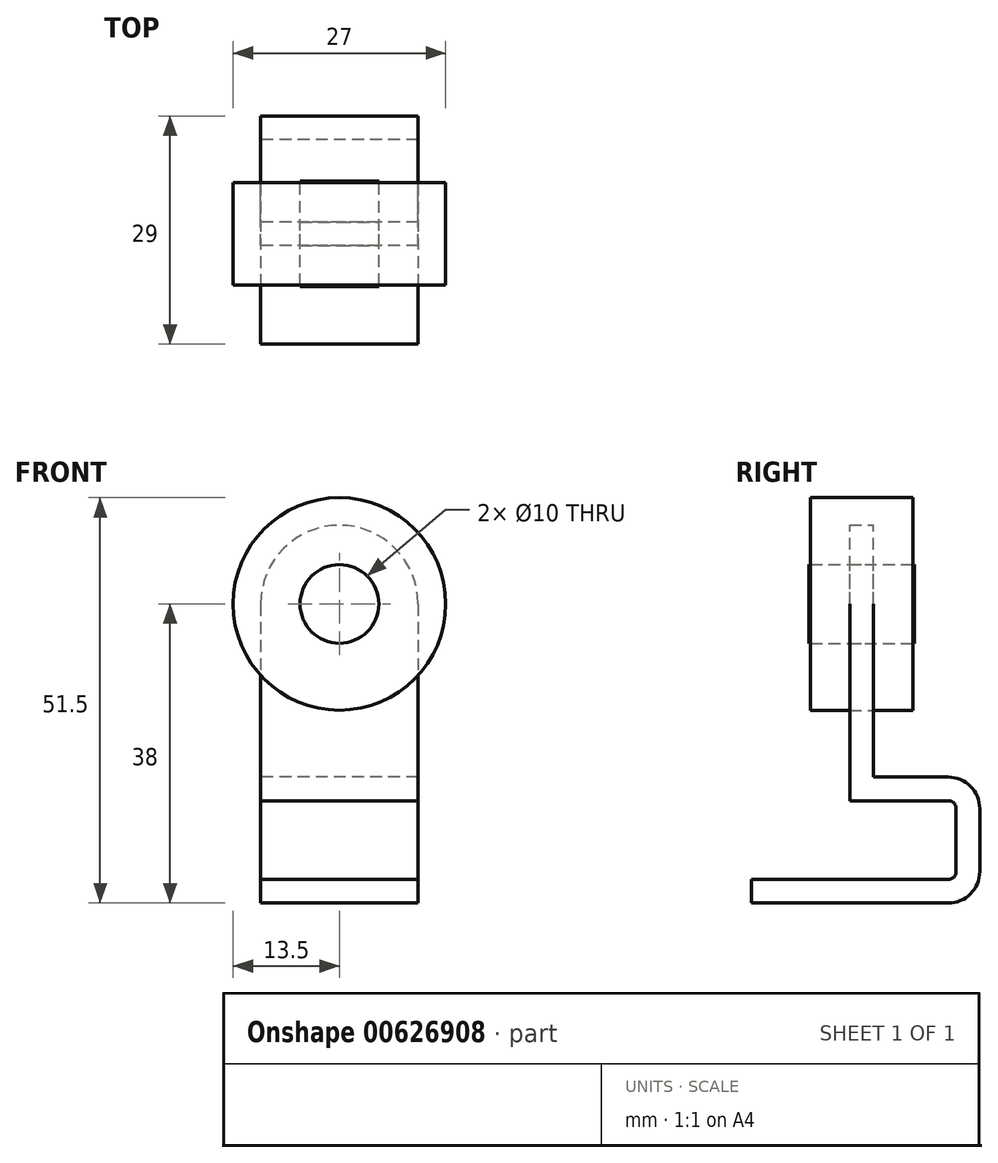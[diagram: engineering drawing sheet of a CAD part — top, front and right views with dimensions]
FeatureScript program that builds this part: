
annotation { "Feature Type Name" : "Feature", "Feature Type Description" : "" }
export const myFeature = defineFeature(function(context is Context, id is Id, definition is map)
    precondition{}
    {
        {
            var Q0;
            Q0=qCreatedBy(makeId("Front.planeOp"),FACE);
            var sketch = newSketch(context, id + "F0", { "sketchPlane" : qUnion([Q0])});
            skCircle(sketch, "E0", {"center": v(0, 0) * mm, "radius": 13.5 * mm});
            skCircle(sketch, "E1", {"center": v(0, 0) * mm, "radius": 5 * mm});
            skSolve(sketch);
        }
        {
            var Q0;
            Q0 = qSketchRegion(id + "F0", true);
            extrude(context, id + "F1", {"entities" : qUnion([Q0]), "depth" : 13 * mm, "offsetDistance" : 25 * mm, "symmetric" : true});
        }
        {
            var Q0;
            Q0=makeQuery(id+"F0.imprint","IMPRINT",FACE,{"disambiguationData":[TD([[makeQuery(id+"F0.imprint","IMPRINT",EDGE,{"derivedFrom":sQuery(id+"F0.wireOp",EDGE,"E1")}),1.0]])]});
            extrude(context, id + "F2", {"entities" : qUnion([Q0]), "depth" : 13.4 * mm, "offsetDistance" : 25 * mm, "symmetric" : true});
        }
        {
            var Q0;
            Q0=qCreatedBy(makeId("Front.planeOp"),FACE);
            var sketch = newSketch(context, id + "F3", { "sketchPlane" : qUnion([Q0])});
            skCircle(sketch, "E2.0", {"center": v(0, 0) * mm, "radius": 5 * mm});
            skArc(sketch, "E3.0", {"start": v(10, 0) * mm, "mid": v(0, 10) * mm, "end": v(-10, 0) * mm});
            skLineSegment(sketch, "E4.top", {"start": v(10, -25) * mm, "end": v(-10, -25) * mm});
            skLineSegment(sketch, "E4.left", {"start": v(10, 0) * mm, "end": v(10, -25) * mm});
            skLineSegment(sketch, "E4.right", {"start": v(-10, 0) * mm, "end": v(-10, -25) * mm});
            skLineSegment(sketch, "E5.bottom", {"start": v(-10, 0) * mm, "end": v(-10, 0) * mm});
            skLineSegment(sketch, "E5.top", {"start": v(-10, 0) * mm, "end": v(-10, 0) * mm});
            skLineSegment(sketch, "E5.left", {"start": v(-10, 0) * mm, "end": v(-10, 0) * mm});
            skLineSegment(sketch, "E5.right", {"start": v(-10, 0) * mm, "end": v(-10, 0) * mm});
            skSolve(sketch);
        }
        {
            var Q0;
            Q0 = qSketchRegion(id + "F3", true);
            extrude(context, id + "F4", {"entities" : qUnion([Q0]), "depth" : 3 * mm, "offsetDistance" : 25 * mm, "symmetric" : true});
        }
        {
            var Q0;
            Q0=qCreatedBy(makeId("Right.planeOp"),FACE);
            var sketch = newSketch(context, id + "F5", { "sketchPlane" : qUnion([Q0])});
            skLineSegment(sketch, "E6", {"start": v(0, -25) * mm, "end": v(11, -25) * mm});
            skLineSegment(sketch, "E7", {"start": v(12, -26) * mm, "end": v(12, -34) * mm});
            skLineSegment(sketch, "E8", {"start": v(11, -35) * mm, "end": v(-14, -35) * mm});
            skLineSegment(sketch, "E9.0.1", {"start": v(1.5, -25) * mm, "end": v(-1.5, -25) * mm});
            skLineSegment(sketch, "E9.0.3", {"start": v(-1.5, -25) * mm, "end": v(1.5, -25) * mm});
            skPoint(sketch, "E10.visualSharp", {"position": v(12, -25) * mm});
            skArc(sketch, "E10.filletArc", {"start": v(12, -26) * mm, "mid": v(11.7, -25.3) * mm, "end": v(11, -25) * mm});
            skPoint(sketch, "E11.visualSharp", {"position": v(12, -35) * mm});
            skArc(sketch, "E11.filletArc", {"start": v(11, -35) * mm, "mid": v(11.7, -34.7) * mm, "end": v(12, -34) * mm});
            skLineSegment(sketch, "E12.0", {"start": v(11, -38) * mm, "end": v(-14, -38) * mm});
            skLineSegment(sketch, "E12.1", {"start": v(0, -22) * mm, "end": v(11, -22) * mm});
            skArc(sketch, "E12.2", {"start": v(15, -26) * mm, "mid": v(13.83, -23.17) * mm, "end": v(11, -22) * mm});
            skLineSegment(sketch, "E12.3", {"start": v(15, -26) * mm, "end": v(15, -34) * mm});
            skArc(sketch, "E12.4", {"start": v(11, -38) * mm, "mid": v(13.83, -36.83) * mm, "end": v(15, -34) * mm});
            skLineSegment(sketch, "E13", {"start": v(-14, -35) * mm, "end": v(-14, -38) * mm});
            skLineSegment(sketch, "E14", {"start": v(0, -22) * mm, "end": v(0, -25) * mm});
            skSolve(sketch);
        }
        {
            var Q0;
            Q0 = qSketchRegion(id + "F5", true);
            extrude(context, id + "F6", {"entities" : qUnion([Q0]), "operationType" : NewBodyOperationType.ADD, "depth" : 20 * mm, "offsetDistance" : 25 * mm, "symmetric" : true});
        }
    });
